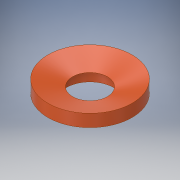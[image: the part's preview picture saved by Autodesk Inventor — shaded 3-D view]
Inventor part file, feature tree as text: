
AUTODESK INVENTOR PART (.ipt)
format: ipt  version: 2017 (Build 210142000, 142)  size: 142,848 bytes
history: native  units: in
note: dims shown in document units (in); Inventor stores cm internally (conversion verified against a paired STEP export)
features: revolve x1, sketch x1
ambient origin geometry x8: Origin, YZ Plane, XZ Plane, XY Plane, X Axis, Y Axis, Z Axis, Center Point
bodies: Body1 (feature_tree)
feature tree (2):
  revolve  "Revolution2"  [1 undecoded]
  sketch  "Sketch1"  dims[d0=0.25in d1=0.1718in d2=15.0deg d4=0.25in d5=1.5in d6=1.25in d7=0.25in d11=0.25in d13=0.5in d15=0.25in d16=0.25in d18=0.125in d19=0.5in d20=0.125in d21=0.25in d22=0.125in d23=0.125in d24=0.25in d25=0.5in d26=2.292in d27=0.5in d29=0.5in d30=90.0deg]
note: 1 required parameter value undecoded (feature->parameter linkage not recoverable at this tier; creation-order binding heuristic only, values carry confidence <= 0.55)
